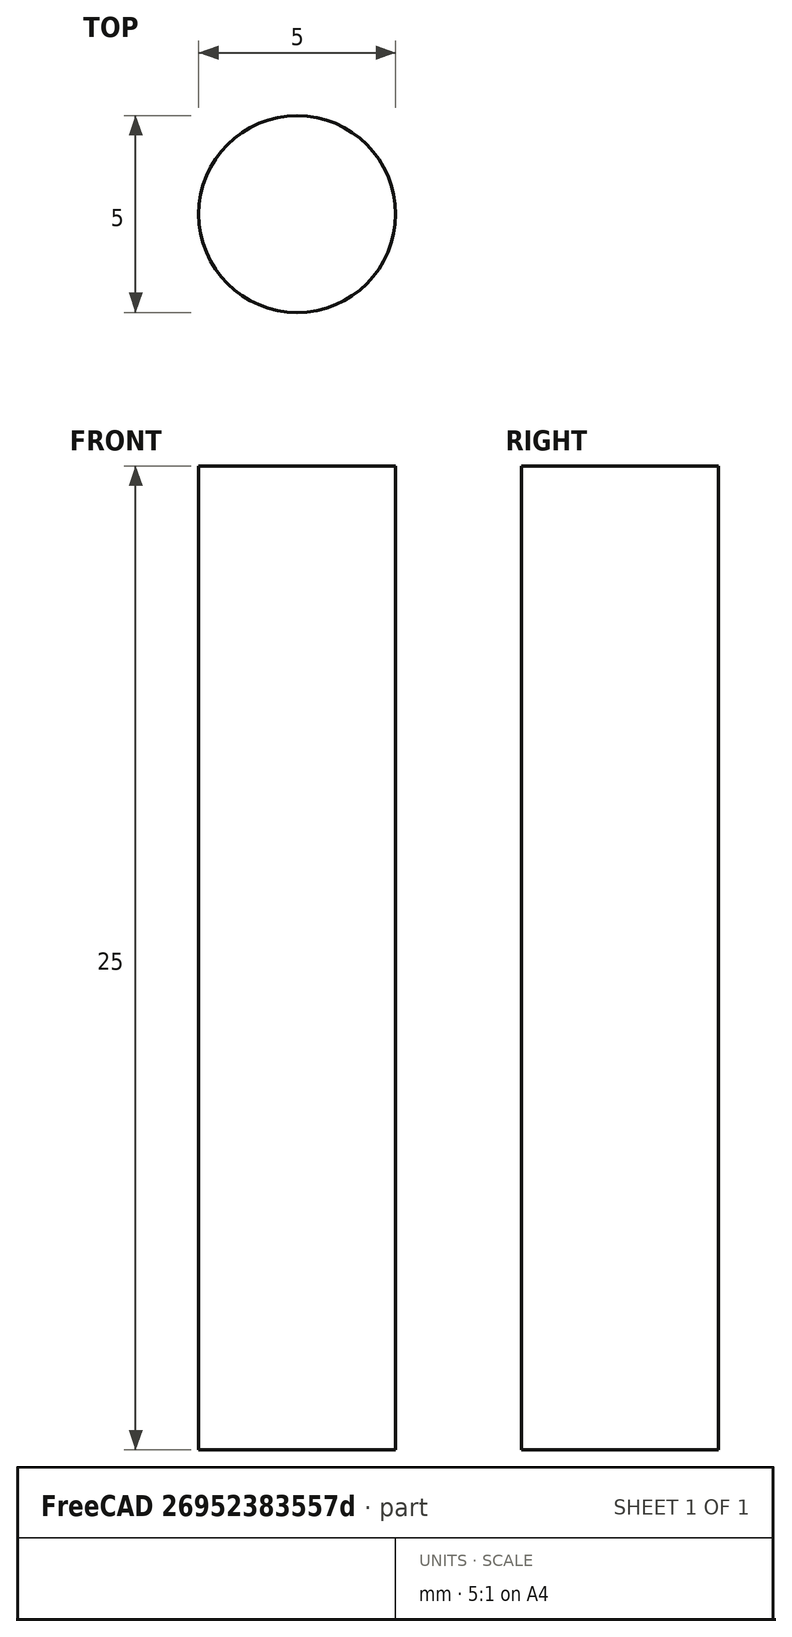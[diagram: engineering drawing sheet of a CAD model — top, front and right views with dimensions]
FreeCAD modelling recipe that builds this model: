
FCSTD DOCUMENT  (FreeCAD 1.0R39319 (Git))
Label: airpod
License: All rights reserved
LicenseURL: https://en.wikipedia.org/wiki/All_rights_reserved
objects: Part::FeaturePython×7, Sketcher::SketchObject×6, Part::Part2DObjectPython×2, Part::Loft×2, Part::Extrusion×2, Part::MultiFuse×2, Part::Mirroring×1, Part::Revolution×1, Part::MultiCommon×1, PartDesign::SubShapeBinder×1, App::DocumentObjectGroup×1
note: 31 computed .brp shape members not serialized (recipe doc carries the construction recipe); baked Part::Feature solids carry a one-line shape summary decoded from their .brp

FEATURE [Sketcher::SketchObject] Sketch  label="Front Profile"
  ArcFitTolerance = 1e-06
  FullyConstrained = true
  MakeInternals = false
  Placement = pos=(0,0,0) rot=(1,0,0;1.5708rad)
  sketch-geometry (9):
    g0-g4: Circle [constr] x5 (B-spline internal-alignment scaffolding for g5; pole/knot coordinates omitted)
    g5: BSplineCurve PolesCount=5 KnotsCount=3 Degree=3 IsPeriodic=0
    g6: GeomPoint [constr] X=-2 Y=0 Z=0
    g7: GeomPoint [constr] X=0 Y=3.5 Z=0
    g8: GeomPoint [constr] X=2 Y=0 Z=0
  constraints (15):
    c: Weight(g0) = 1
    c: Equal(g0, g1-g4) x4
    c: InternalAlignment(g0-g4 -> g5) x5
    c: InternalAlignment(g6,g5)
    c: InternalAlignment(g7,g5)
    c: InternalAlignment(g8,g5)
    c: PointOnObject(g0,g-1)
    c: PointOnObject(g4,g-1)
    c: Horizontal(g1,g3)
    c: Vertical(g1,g5)
    c: Vertical(g3,g5)
    c: DistanceX(g1,g3) = 4
    c: DistanceY(g-1,g1) = 3.5
    c: PointOnObject(g2,g-2)
    c: Coincident(g7,g2)
FEATURE [Sketcher::SketchObject] Sketch001  label="Mid_profile"
  ArcFitTolerance = 1e-06
  FullyConstrained = true
  MakeInternals = false
  Placement = pos=(0,8,0) rot=(1,0,0;1.5708rad)
  sketch-geometry (5):
    g0: ArcOfEllipse CenterX=0 CenterY=0 CenterZ=0 NormalX=0 NormalY=0 NormalZ=1 MajorRadius=7.5 MinorRadius=5 AngleXU=1.5708 StartAngle=4.71239 EndAngle=7.85398
    g1: LineSegment [constr] StartX=0 StartY=7.5 StartZ=0 EndX=0 EndY=-7.5 EndZ=0
    g2: LineSegment [constr] StartX=-5 StartY=0 StartZ=0 EndX=5 EndY=0 EndZ=0
    g3: GeomPoint [constr] X=0 Y=5.59017 Z=0
    g4: GeomPoint [constr] X=0 Y=-5.59017 Z=0
  constraints (7):
    c: InternalAlignment(g1-g4 -> g0) x4
    c: Coincident(g0,g-1)
    c: PointOnObject(g0,g2)
    c: DistanceX(g0,g0) = 10
    c: DistanceY(g-1,g1) = 7.5
    c: Horizontal(g2)
    c: PointOnObject(g0,g2)
FEATURE [Part::Part2DObjectPython] Clone2D  label="End_profile"  # Draft 2D object (typed FeaturePython)
  Fuse = false
  Objects = -> [Sketch001]
  Placement = pos=(0,10,0) rot=(1,0,0;1.5708rad)
  Scale = (1,1,1)
FEATURE [Part::Loft] Loft
  Closed = false
  MaxDegree = 5
  Ruled = false
  Sections = -> [Sketch,Sketch001,Clone2D]
  Solid = false
FEATURE [Part::Mirroring] Part__Mirroring  label="Loft (Mirror #1)"
  Base = (0,0,0)
  Normal = (0,0,1)
  Source = -> Loft
FEATURE [Sketcher::SketchObject] Sketch002  label="ref_line"
  ArcFitTolerance = 1e-06
  ExternalGeometry = -> [Clone2D,Part__Mirroring]
  FullyConstrained = true
  MakeInternals = false
  sketch-geometry (1):
    g0: LineSegment StartX=-5 StartY=10 StartZ=0 EndX=5 EndY=10 EndZ=0
  constraints (2):
    c: Coincident(g0,g-3)
    c: Coincident(g0,g-4)
FEATURE [Part::Revolution] Revolve
  Angle = -180
  Axis = (1,0,0)
  AxisLink = -> Sketch002 [Edge1]
  Base = (5,10,0)
  FaceMakerClass = Part::FaceMakerBullseye
  Solid = false
  Source = -> Clone2D
  Symmetric = false
FEATURE [Sketcher::SketchObject] Sketch003
  ArcFitTolerance = 1e-06
  FullyConstrained = false
  MakeInternals = false
  sketch-geometry (9):
    g0-g4: Circle [constr] x5 (B-spline internal-alignment scaffolding for g5; pole/knot coordinates omitted)
    g5: BSplineCurve PolesCount=5 KnotsCount=3 Degree=3 IsPeriodic=0
    g6: GeomPoint [constr] X=1.80743 Y=17.7931 Z=0
    g7: GeomPoint [constr] X=3.08465 Y=3.84068 Z=0
    g8: GeomPoint [constr] X=5.42892 Y=0.591039 Z=0
  constraints (6):
    c: Weight(g0) = 1
    c: Equal(g0, g1-g4) x4
    c: InternalAlignment(g0-g4 -> g5) x5
    c: InternalAlignment(g6,g5)
    c: InternalAlignment(g7,g5)
    c: InternalAlignment(g8,g5)
FEATURE [Part::Extrusion] Extrude
  Base = -> Sketch003
  Dir = (0,0,1)
  DirMode = 2
  FaceMakerClass = Part::FaceMakerBullseye
  FaceMakerMode = 3
  LengthFwd = 20
  LengthRev = 0
  Solid = false
  Symmetric = true
FEATURE [Part::MultiCommon] Common
  Refine = true
  Shapes = -> [Loft]
FEATURE [Part::MultiFuse] Fusion
  Refine = true
  Shapes = -> [Common,Part__Mirroring,Revolve]
FEATURE [Part::FeaturePython] Slice  # WARN: FeaturePython — macro-defined, semantics opaque (R4)
  Base = -> Fusion
  Mode = 1
  Tolerance = 0
  Tools = -> [Extrude]
FEATURE [Part::FeaturePython] Slice_child0  label="Slice.0"  # WARN: FeaturePython — macro-defined, semantics opaque (R4)
  Base = -> Slice
  FilterType = 1
  Invert = false
  OverrideMaxVal = 0
  WindowFrom = 80
  WindowTo = 100
  items = 0
FEATURE [Part::FeaturePython] Slice_child1  label="Slice.1"  # WARN: FeaturePython — macro-defined, semantics opaque (R4)
  Base = -> Slice
  FilterType = 1
  Invert = false
  OverrideMaxVal = 0
  WindowFrom = 80
  WindowTo = 100
  items = 1
FEATURE [Part::FeaturePython] Slice_child2  label="Slice.2"  # WARN: FeaturePython — macro-defined, semantics opaque (R4)
  Base = -> Slice
  FilterType = 1
  Invert = false
  OverrideMaxVal = 0
  WindowFrom = 80
  WindowTo = 100
  items = 2
FEATURE [Part::FeaturePython] Slice_child3  label="Slice.3"  # WARN: FeaturePython — macro-defined, semantics opaque (R4)
  Base = -> Slice
  FilterType = 1
  Invert = false
  OverrideMaxVal = 0
  WindowFrom = 80
  WindowTo = 100
  items = 3
FEATURE [Part::FeaturePython] Slice_child4  label="Slice.4"  # WARN: FeaturePython — macro-defined, semantics opaque (R4)
  Base = -> Slice
  FilterType = 1
  Invert = false
  OverrideMaxVal = 0
  WindowFrom = 80
  WindowTo = 100
  items = 4
FEATURE [Part::FeaturePython] Slice_child5  label="Slice.5"  # WARN: FeaturePython — macro-defined, semantics opaque (R4)
  Base = -> Slice
  FilterType = 1
  Invert = false
  OverrideMaxVal = 0
  WindowFrom = 80
  WindowTo = 100
  items = 5
FEATURE [Sketcher::SketchObject] Sketch004
  ArcFitTolerance = 1e-06
  AttachmentSupport = -> [Slice_child4]
  FullyConstrained = true
  MakeInternals = false
  MapMode = 45
  Placement = pos=(3.54146,13.1422,5.00445e-09) rot=(0.463452,0.626583,0.626583;2.27362rad)
FEATURE [Sketcher::SketchObject] Sketch005
  ArcFitTolerance = 1e-06
  FullyConstrained = true
  MakeInternals = false
  Placement = pos=(0,0,-5) rot=(0,0,1;0rad)
  sketch-geometry (1):
    g0: Circle CenterX=10 CenterY=12 CenterZ=0 NormalX=0 NormalY=0 NormalZ=1 AngleXU=0 Radius=2.5
  constraints (3):
    c: Diameter(g0) = 5
    c: Distance(g0,g-1) = 12
    c: Distance(g0,g-2) = 10
FEATURE [Part::Extrusion] Extrude002
  Base = -> Sketch005
  Dir = (0,0,1)
  DirMode = 2
  FaceMakerClass = Part::FaceMakerBullseye
  FaceMakerMode = 3
  LengthFwd = -25
  LengthRev = 0
  Solid = true
  Symmetric = false
FEATURE [PartDesign::SubShapeBinder] Binder
  BindCopyOnChange = 0
  BindMode = 0
  ClaimChildren = false
  Fuse = false
  MakeFace = true
  OffsetFill = false
  OffsetIntersection = false
  OffsetJoinType = 0
  OffsetOpenResult = false
  PartialLoad = false
  Refine = true
  Relative = true
  Support = -> [Slice_child2[Edge3],Slice_child5[Edge4],Slice_child0[Edge3]]
  _Version = 2
FEATURE [Part::Part2DObjectPython] Clone2D001  label="Sketch005 (2D)"  # Draft 2D object (typed FeaturePython)
  Fuse = false
  Objects = -> [Sketch005]
  Placement = pos=(0,0,-5) rot=(0,1,0;5.95157rad)
  Scale = (1,1,1)
FEATURE [Part::Loft] Loft001
  Closed = false
  MaxDegree = 5
  Ruled = false
  Sections = -> [Sketch005,Clone2D001,Binder]
  Solid = false
FEATURE [Part::MultiFuse] Fusion001
  Refine = true
  Shapes = -> [Loft001,Slice_child3,Slice_child4]
FEATURE [App::DocumentObjectGroup] GrExplode_Slice  label="Exploded Slice"
  Group = -> [Slice_child0,Slice_child1,Slice_child2,Slice_child5,Sketch004,Fusion001]
